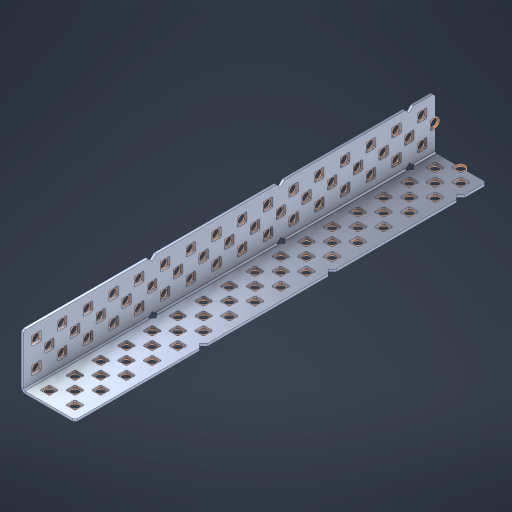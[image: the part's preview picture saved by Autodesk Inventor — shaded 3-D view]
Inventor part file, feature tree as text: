
AUTODESK INVENTOR PART (.ipt)
format: ipt  version: 2023 (Build 270158000, 158)  size: 1,319,424 bytes
history: native  units: in
note: dims shown in document units (in); Inventor stores cm internally (conversion verified against a paired STEP export)
features: other x102, extrude x94, sheet_metal_op x8, sketch x7, pattern_linear x2, mirror x1, chamfer x1
ambient origin geometry x8: Origin, YZ Plane, XZ Plane, XY Plane, X Axis, Y Axis, Z Axis, Center Point
bodies: Solid1 (feature_tree), Body (feature_tree)
feature tree (215):
  sheet_metal_op  "Flanges"
  sheet_metal_op  "Body Pattern"
  pattern_linear  "Center Pattern"  Spacing1=1.0in  [1 undecoded]
  other  "Arc Length"
  pattern_linear  "Notch Pattern"  Spacing1=0.1875in  [1 undecoded]
  other  "Diagonal Plane"
  mirror  "Everything Mirrored"
  chamfer  "End Chamfer"
  sketch  "Sketch1"  dims[d0=1.0in]
  other  "Plate1"
  sketch  "Sketch2"  dims[d1=8.0in]
  other  "Plate2"
  sheet_metal_op  "Bend1"
  sheet_metal_op  "Corner1"
  sketch  "Sketch8"  dims[d2=0.0469in]
  sketch  "Sketch9"  dims[d3=0.0469in]
  other  "Srf91"
  sheet_metal_op  "Body Pattern Sketch"
  other  "Srf92"
  sketch  "Sketch13"  dims[d4=0.0234in]
  sketch  "Sketch15"  dims[d5=0.0938in]
  sketch  "Sketch16"  dims[d6=0.0469in d7=1.0in d8=90.0deg d9=0.0312in d10=0.1875in d11=0.0469in d12=0.0469in d49=0.182in d50=0.02in d52=0.25in d53=0.0469in d54=0.0in d55=0.172in d56=1.0in d57=0.0in d60=6.2992in d62=0.5in d63=0.7874in d65=0.5in d85=0.1473in d86=0.1659in d89=0.0469in d90=0.0in d91=0.04in d92=0.0491in d95=2.5in d96=0.04in d97=0.25in d98=45.0deg d99=0.25in d106=0.182in d107=0.02in d108=0.5in d110=0.0469in d111=0.0in d112=0.172in d113=0.5in d114=0.0in d117=0.5in d123=0.25in d125=0.25in d126=0.0491in d127=0.1227in d128=0.08in d129=0.04in d130=2.5in]
  other  "Srf786"
  other  "Srf856"
  other  "Srf857"
  other  "Srf858"
  other  "Srf859"
  other  "Srf860"
  other  "Srf861"
  other  "Srf889"
  other  "Srf890"
  other  "Srf891"
  other  "Srf1275"
  other  "Srf1276"
  other  "Srf1278"
  other  "Srf1279"
  other  "Srf1280"
  other  "Srf1281"
  other  "Srf1282"
  other  "Srf1283"
  other  "Srf1277"
  other  "Srf1285"
  other  "Srf1286"
  other  "Srf1287"
  other  "Srf1383"
  other  "Srf1384"
  other  "Srf1385"
  other  "Srf1386"
  other  "Srf1387"
  other  "Srf1388"
  other  "Srf1389"
  other  "Srf1390"
  other  "Srf1391"
  other  "Srf1392"
  other  "Srf1393"
  other  "Srf1394"
  other  "Srf1395"
  other  "Srf1396"
  other  "Srf1397"
  other  "Srf1398"
  other  "Srf1399"
  other  "Srf1400"
  other  "Srf1401"
  other  "Srf1402"
  other  "Srf1403"
  other  "Srf1404"
  other  "Srf1405"
  other  "Srf1406"
  other  "Srf1445"
  other  "Srf1446"
  other  "Srf1447"
  other  "Srf1448"
  other  "Srf1449"
  other  "Srf1450"
  other  "Srf1451"
  other  "Srf1452"
  other  "Srf1453"
  other  "Srf1454"
  other  "Srf1455"
  other  "Srf1456"
  other  "Srf1475"
  other  "Srf1476"
  other  "Srf1477"
  other  "Srf1478"
  other  "Srf1479"
  other  "Srf1480"
  other  "Srf1481"
  other  "Srf1482"
  other  "Srf1483"
  other  "Srf1484"
  other  "Srf1485"
  other  "Srf1486"
  other  "Srf1487"
  other  "Srf1488"
  other  "Srf1489"
  other  "Srf1490"
  other  "Srf1491"
  other  "Srf1492"
  other  "Srf1493"
  other  "Srf1494"
  other  "Srf1495"
  other  "Srf1496"
  other  "Srf1497"
  other  "Srf1498"
  other  "Srf1537"
  other  "Srf1538"
  other  "Srf1539"
  other  "Srf1540"
  other  "Srf1541"
  other  "Srf1542"
  other  "Srf1543"
  other  "Srf1544"
  other  "Srf1545"
  other  "Srf1546"
  other  "Srf1547"
  other  "Srf1548"
  sheet_metal_op  "Body Stamp"
  sheet_metal_op  "Body Circle"
  other  "Center Stamp"
  other  "Center Circle"
  sheet_metal_op  "Notch"
  extrude  "ExtrusionSrf92"  Depth=0.0469in
  extrude  "ExtrusionSrf856"  Depth=0.0469in
  extrude  "ExtrusionSrf857"  Depth=0.182in
  extrude  "ExtrusionSrf858"  Depth=0.02in
  extrude  "ExtrusionSrf859"  Depth=0.25in
  extrude  "ExtrusionSrf860"  Depth=0.0469in
  extrude  "ExtrusionSrf861"  TaperAngle=0.0deg  [1 undecoded]
  extrude  "ExtrusionSrf889"  Depth=2.5in
  extrude  "ExtrusionSrf890"  Depth=1.0in TaperAngle=0.0deg
  extrude  "ExtrusionSrf891"  Depth=2.5in
  extrude  "ExtrusionSrf1275"  Depth=0.5in
  extrude  "ExtrusionSrf1276"  Depth=2.5in
  extrude  "ExtrusionSrf1277"  Depth=2.5in
  extrude  "ExtrusionSrf1278"  Depth=0.0469in
  extrude  "ExtrusionSrf1279"  Depth=2.5in TaperAngle=0.0deg
  extrude  "ExtrusionSrf1280"  Depth=2.5in
  extrude  "ExtrusionSrf1281"  Depth=0.25in TaperAngle=45.0deg
  extrude  "ExtrusionSrf1282"  Depth=0.25in
  extrude  "ExtrusionSrf1345"  Depth=0.182in
  extrude  "ExtrusionSrf1346"  Depth=0.02in
  extrude  "ExtrusionSrf1347"  Depth=0.5in
  extrude  "ExtrusionSrf1348"  Depth=0.0469in
  extrude  "ExtrusionSrf1383"  TaperAngle=0.0deg  [1 undecoded]
  extrude  "ExtrusionSrf1384"  Depth=2.5in
  extrude  "ExtrusionSrf1385"  Depth=0.5in TaperAngle=0.0deg
  extrude  "ExtrusionSrf1386"  Depth=0.5in
  extrude  "ExtrusionSrf1387"  Depth=0.25in
  extrude  "ExtrusionSrf1388"  Depth=0.25in
  extrude  "ExtrusionSrf1389"  Depth=2.5in
  extrude  "ExtrusionSrf1390"  Depth=2.5in
  extrude  "ExtrusionSrf1391"  Depth=2.5in
  extrude  "ExtrusionSrf1392"  Depth=2.5in
  extrude  "ExtrusionSrf1393"  Depth=2.5in
  extrude  "ExtrusionSrf1394"  [1 undecoded]
  extrude  "ExtrusionSrf1395"  [1 undecoded]
  extrude  "ExtrusionSrf1396"  [1 undecoded]
  extrude  "ExtrusionSrf1397"  [1 undecoded]
  extrude  "ExtrusionSrf1398"  [1 undecoded]
  extrude  "ExtrusionSrf1399"  [1 undecoded]
  extrude  "ExtrusionSrf1400"  [1 undecoded]
  extrude  "ExtrusionSrf1401"  [1 undecoded]
  extrude  "ExtrusionSrf1402"  [1 undecoded]
  extrude  "ExtrusionSrf1403"  [1 undecoded]
  extrude  "ExtrusionSrf1404"  [1 undecoded]
  extrude  "ExtrusionSrf1405"  [1 undecoded]
  extrude  "ExtrusionSrf1406"  [1 undecoded]
  extrude  "ExtrusionSrf1445"  [1 undecoded]
  extrude  "ExtrusionSrf1446"  [1 undecoded]
  extrude  "ExtrusionSrf1447"  [1 undecoded]
  extrude  "ExtrusionSrf1448"  [1 undecoded]
  extrude  "ExtrusionSrf1449"  [1 undecoded]
  extrude  "ExtrusionSrf1450"  [1 undecoded]
  extrude  "ExtrusionSrf1451"  [1 undecoded]
  extrude  "ExtrusionSrf1452"  [1 undecoded]
  extrude  "ExtrusionSrf1453"  [1 undecoded]
  extrude  "ExtrusionSrf1454"  [1 undecoded]
  extrude  "ExtrusionSrf1455"  [1 undecoded]
  extrude  "ExtrusionSrf1456"  [1 undecoded]
  extrude  "ExtrusionSrf1475"  [1 undecoded]
  extrude  "ExtrusionSrf1476"  [1 undecoded]
  extrude  "ExtrusionSrf1477"  [1 undecoded]
  extrude  "ExtrusionSrf1478"  [1 undecoded]
  extrude  "ExtrusionSrf1479"  [1 undecoded]
  extrude  "ExtrusionSrf1480"  [1 undecoded]
  extrude  "ExtrusionSrf1481"  [1 undecoded]
  extrude  "ExtrusionSrf1482"  [1 undecoded]
  extrude  "ExtrusionSrf1483"  [1 undecoded]
  extrude  "ExtrusionSrf1484"  [1 undecoded]
  extrude  "ExtrusionSrf1485"  [1 undecoded]
  extrude  "ExtrusionSrf1486"  [1 undecoded]
  extrude  "ExtrusionSrf1487"  [1 undecoded]
  extrude  "ExtrusionSrf1488"  [1 undecoded]
  extrude  "ExtrusionSrf1489"  [1 undecoded]
  extrude  "ExtrusionSrf1490"  [1 undecoded]
  extrude  "ExtrusionSrf1491"  [1 undecoded]
  extrude  "ExtrusionSrf1492"  [1 undecoded]
  extrude  "ExtrusionSrf1493"  [1 undecoded]
  extrude  "ExtrusionSrf1494"  [1 undecoded]
  extrude  "ExtrusionSrf1495"  [1 undecoded]
  extrude  "ExtrusionSrf1496"  [1 undecoded]
  extrude  "ExtrusionSrf1497"  [1 undecoded]
  extrude  "ExtrusionSrf1498"  [1 undecoded]
  extrude  "ExtrusionSrf1537"  [1 undecoded]
  extrude  "ExtrusionSrf1538"  [1 undecoded]
  extrude  "ExtrusionSrf1539"  [1 undecoded]
  extrude  "ExtrusionSrf1540"  [1 undecoded]
  extrude  "ExtrusionSrf1541"  [1 undecoded]
  extrude  "ExtrusionSrf1542"  [1 undecoded]
  extrude  "ExtrusionSrf1543"  [1 undecoded]
  extrude  "ExtrusionSrf1544"  [1 undecoded]
  extrude  "ExtrusionSrf1545"  [1 undecoded]
  extrude  "ExtrusionSrf1546"  [1 undecoded]
  extrude  "ExtrusionSrf1547"  [1 undecoded]
  extrude  "ExtrusionSrf1548"  [1 undecoded]
note: 65 required parameter values undecoded (feature->parameter linkage not recoverable at this tier; creation-order binding heuristic only, values carry confidence <= 0.55)
